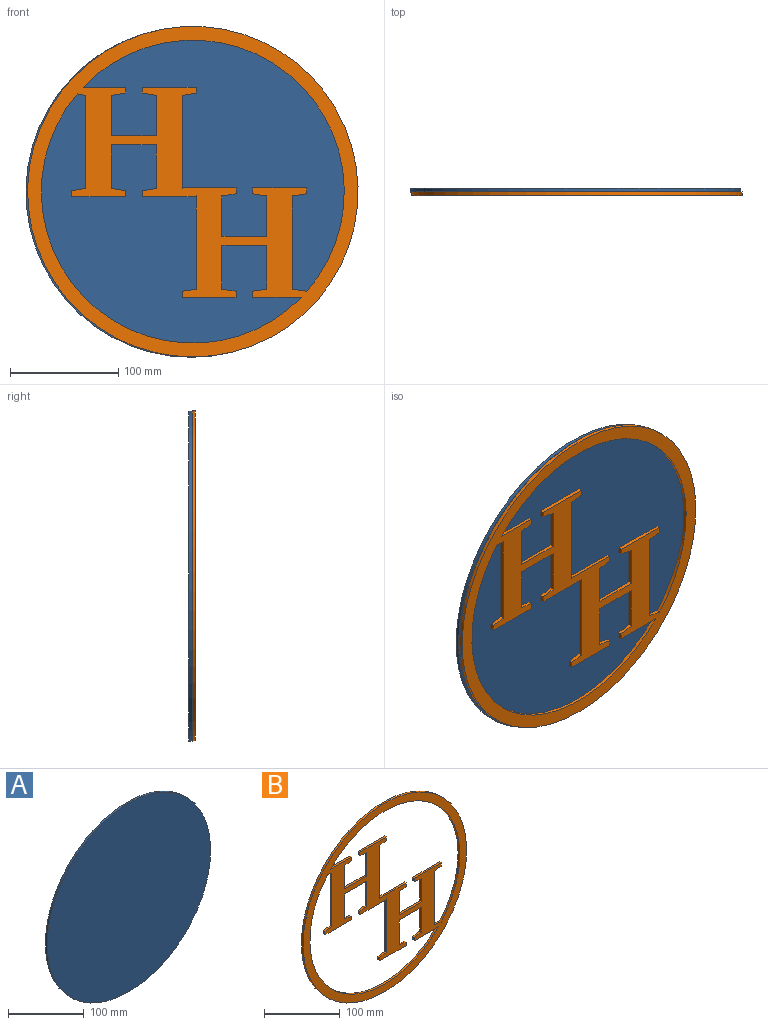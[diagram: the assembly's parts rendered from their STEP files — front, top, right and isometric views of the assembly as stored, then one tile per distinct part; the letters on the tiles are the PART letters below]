
ASSEMBLY  parts=2 mates=1
PART A: 3 faces, bbox 304.8x3.2x304.8 mm
  f0: cylinder r=152.4mm len=304.8mm, axis (0,1,0), area 3040.2mm2, adj f1,f2
  f1: plane 304.8x304.8mm, normal (0,-1,0), area 72965.9mm2, adj f0
  f2: plane 304.8x304.8mm, normal (0,1,0), area 72965.9mm2, adj f0
PART B: 60 faces, bbox 304.8x3.2x304.8 mm
  f0: cylinder r=139.7mm len=239.82mm, axis (0,1,0), area 1361.8mm2, adj f1,f55,f58,f59
  f1: plane 8.09x3.18mm, normal (-0.16,0,-0.99), area 26mm2, adj f0,f2,f58,f59
  f2: plane 85.88x3.18mm, normal (-1,0,0), area 272.7mm2, adj f1,f3,f58,f59
  f3: plane 12.96x3.18mm, normal (-0.15,0,0.99), area 41.6mm2, adj f2,f4,f58,f59
  f4: plane 5.56x3.18mm, normal (-1,0,0), area 17.7mm2, adj f3,f5,f58,f59
  f5: plane 49.62x3.18mm, normal (0,0,-1), area 157.6mm2, adj f4,f6,f58,f59
  f6: plane 5.56x3.18mm, normal (1,0,0), area 17.7mm2, adj f5,f7,f58,f59
  f7: plane 12.96x3.18mm, normal (0.15,0,0.99), area 41.6mm2, adj f6,f8,f58,f59
  f8: plane 40.25x3.18mm, normal (1,0,0), area 127.8mm2, adj f7,f9,f58,f59
  f9: plane 41.27x3.18mm, normal (0,0,-1), area 131mm2, adj f8,f10,f58,f59
  f10: plane 40.25x3.18mm, normal (-1,0,0), area 127.8mm2, adj f9,f11,f58,f59
  f11: plane 12.96x3.18mm, normal (-0.15,0,0.99), area 41.6mm2, adj f10,f12,f58,f59
  f12: plane 5.56x3.18mm, normal (-1,0,0), area 17.7mm2, adj f11,f13,f58,f59
  f13: plane 49.77x3.18mm, normal (0,0,-1), area 158mm2, adj f12,f14,f58,f59
  f14: plane 3.18x0.65mm, normal (1,0,0), area 2.1mm2, adj f13,f15,f58,f59
  f15: plane 3.18x0.1mm, normal (-0.16,0,-0.99), area 0.3mm2, adj f14,f16,f58,f59
  f16: plane 85.88x3.18mm, normal (-1,0,0), area 272.7mm2, adj f15,f17,f58,f59
  f17: plane 12.96x3.18mm, normal (-0.15,0,0.99), area 41.6mm2, adj f16,f18,f58,f59
  f18: plane 5.56x3.18mm, normal (-1,0,0), area 17.7mm2, adj f17,f19,f58,f59
  f19: plane 49.62x3.18mm, normal (0,0,-1), area 157.6mm2, adj f18,f20,f58,f59
  f20: plane 5.56x3.18mm, normal (1,0,0), area 17.7mm2, adj f19,f21,f58,f59
  f21: plane 12.96x3.18mm, normal (0.15,0,0.99), area 41.6mm2, adj f20,f22,f58,f59
  f22: plane 40.25x3.18mm, normal (1,0,0), area 127.8mm2, adj f21,f23,f58,f59
  f23: plane 41.27x3.18mm, normal (0,0,-1), area 131mm2, adj f22,f24,f58,f59
  f24: plane 40.25x3.18mm, normal (-1,0,0), area 127.8mm2, adj f23,f25,f58,f59
  f25: plane 12.96x3.18mm, normal (-0.15,0,0.99), area 41.6mm2, adj f24,f26,f58,f59
  f26: plane 5.56x3.18mm, normal (-1,0,0), area 17.7mm2, adj f25,f55,f58,f59
  f27: plane 39.14x3.18mm, normal (0,0,1), area 124.3mm2, adj f28,f56,f58,f59
  f28: cylinder r=139.7mm len=240.89mm, axis (0,1,0), area 1375.8mm2, adj f27,f29,f58,f59
  f29: plane 3.18x0.35mm, normal (1,0,0), area 1.1mm2, adj f28,f30,f58,f59
  f30: plane 13.03x3.18mm, normal (0.15,0,0.99), area 41.9mm2, adj f29,f31,f58,f59
  f31: plane 85.88x3.18mm, normal (1,0,0), area 272.7mm2, adj f30,f32,f58,f59
  f32: plane 13.03x3.18mm, normal (0.16,0,-0.99), area 41.9mm2, adj f31,f33,f58,f59
  f33: plane 5.49x3.18mm, normal (1,0,0), area 17.4mm2, adj f32,f34,f58,f59
  f34: plane 49.77x3.18mm, normal (0,0,1), area 158mm2, adj f33,f35,f58,f59
  f35: plane 5.49x3.18mm, normal (-1,0,0), area 17.4mm2, adj f34,f36,f58,f59
  f36: plane 12.96x3.18mm, normal (-0.16,0,-0.99), area 41.7mm2, adj f35,f37,f58,f59
  f37: plane 37.34x3.18mm, normal (-1,0,0), area 118.6mm2, adj f36,f38,f58,f59
  f38: plane 41.27x3.18mm, normal (0,0,1), area 131mm2, adj f37,f39,f58,f59
  f39: plane 37.34x3.18mm, normal (1,0,0), area 118.6mm2, adj f38,f40,f58,f59
  f40: plane 12.96x3.18mm, normal (0.16,0,-0.99), area 41.7mm2, adj f39,f41,f58,f59
  f41: plane 5.49x3.18mm, normal (1,0,0), area 17.4mm2, adj f40,f42,f58,f59
  f42: plane 49.62x3.18mm, normal (0,0,1), area 157.6mm2, adj f41,f43,f58,f59
  f43: plane 3.18x0.67mm, normal (-1,0,0), area 2.1mm2, adj f42,f44,f58,f59
  f44: plane 3.18x0.17mm, normal (0.15,0,0.99), area 0.5mm2, adj f43,f45,f58,f59
  f45: plane 85.88x3.18mm, normal (1,0,0), area 272.7mm2, adj f44,f46,f58,f59
  f46: plane 13.03x3.18mm, normal (0.16,0,-0.99), area 41.9mm2, adj f45,f47,f58,f59
  f47: plane 5.49x3.18mm, normal (1,0,0), area 17.4mm2, adj f46,f48,f58,f59
  f48: plane 49.77x3.18mm, normal (0,0,1), area 158mm2, adj f47,f49,f58,f59
  f49: plane 5.49x3.18mm, normal (-1,0,0), area 17.4mm2, adj f48,f50,f58,f59
  f50: plane 12.96x3.18mm, normal (-0.16,0,-0.99), area 41.7mm2, adj f49,f51,f58,f59
  f51: plane 37.34x3.18mm, normal (-1,0,0), area 118.6mm2, adj f50,f52,f58,f59
  f52: plane 41.27x3.18mm, normal (0,0,1), area 131mm2, adj f51,f53,f58,f59
  f53: plane 37.34x3.18mm, normal (1,0,0), area 118.6mm2, adj f52,f54,f58,f59
  f54: plane 12.96x3.18mm, normal (0.16,0,-0.99), area 41.7mm2, adj f53,f56,f58,f59
  f55: plane 44.95x3.18mm, normal (0,0,-1), area 142.7mm2, adj f0,f26,f58,f59
  f56: plane 5.49x3.18mm, normal (1,0,0), area 17.4mm2, adj f27,f54,f58,f59
  f57: cylinder r=152.4mm len=304.8mm, axis (0,1,0), area 3040.2mm2, adj f58,f59
  f58: plane 304.8x304.8mm, normal (0,-1,0), area 23161.4mm2, adj f0,f1,f2,f3,f4,f5,f6,f7
  f59: plane 304.8x304.8mm, normal (0,1,0), area 23161.4mm2, adj f0,f1,f2,f3,f4,f5,f6,f7
PLACE A t=(-92.88,-62.4,-21.78)mm
PLACE B t=(-91.36,-65.57,-21.4)mm
MATE fastened A.f0 <-> B.f59  axis (0,-1,0) through (-92.88,-65.57,-21.78)mm
